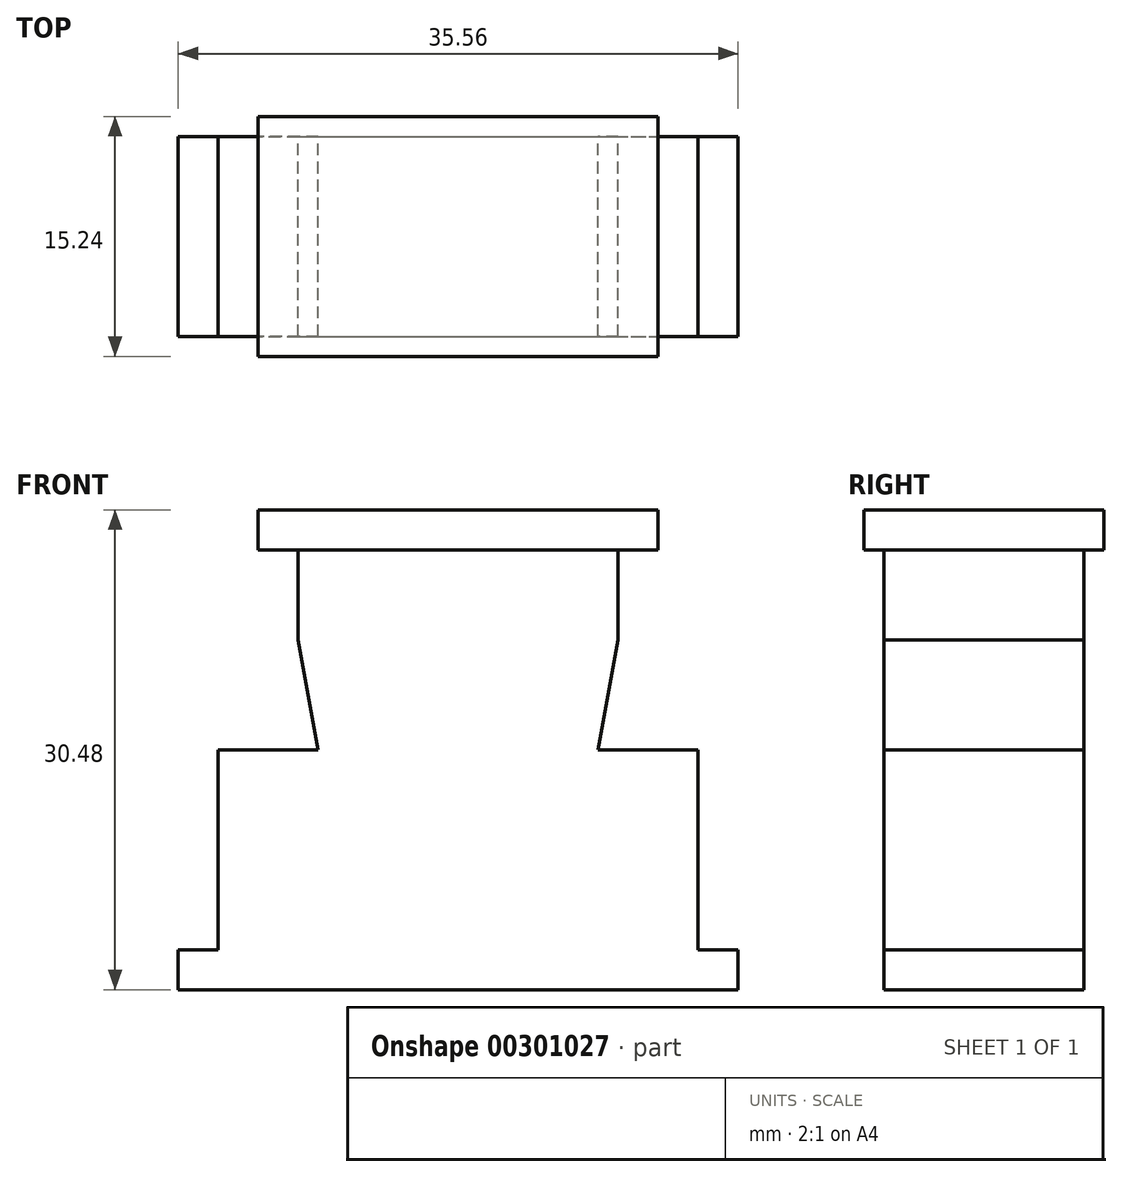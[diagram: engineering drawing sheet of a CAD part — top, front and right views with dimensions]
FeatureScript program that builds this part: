
annotation { "Feature Type Name" : "Feature", "Feature Type Description" : "" }
export const myFeature = defineFeature(function(context is Context, id is Id, definition is map)
    precondition{}
    {
        {
            var Q0;
            Q0=qCreatedBy(makeId("Front.planeOp"),FACE);
            var sketch = newSketch(context, id + "F0", { "sketchPlane" : qUnion([Q0])});
            skLineSegment(sketch, "E0.bottom", {"start": v(0, 19.46) * mm, "end": v(-25.4, 19.46) * mm});
            skLineSegment(sketch, "E0.top", {"start": v(0, 16.92) * mm, "end": v(-25.4, 16.92) * mm});
            skLineSegment(sketch, "E0.left", {"start": v(0, 19.46) * mm, "end": v(0, 16.92) * mm});
            skLineSegment(sketch, "E0.right", {"start": v(-25.4, 19.46) * mm, "end": v(-25.4, 16.92) * mm});
            skLineSegment(sketch, "E1", {"start": v(-12.7, 16.92) * mm, "end": v(-12.7, -8.48) * mm});
            skLineSegment(sketch, "E2", {"start": v(-12.7, -8.48) * mm, "end": v(-12.7, 4.22) * mm});
            skLineSegment(sketch, "E3", {"start": v(-22.86, 11.2) * mm, "end": v(-2.54, 11.2) * mm});
            skPoint(sketch, "E4", {"position": v(-12.7, 11.2) * mm});
            skLineSegment(sketch, "E5", {"start": v(-12.7, -8.48) * mm, "end": v(-30.48, -8.48) * mm});
            skLineSegment(sketch, "E6", {"start": v(-30.48, -8.48) * mm, "end": v(5.08, -8.48) * mm});
            skLineSegment(sketch, "E7", {"start": v(-30.48, -8.48) * mm, "end": v(-30.48, -11.02) * mm});
            skLineSegment(sketch, "E8", {"start": v(-30.48, -11.02) * mm, "end": v(5.07, -11.02) * mm});
            skLineSegment(sketch, "E9", {"start": v(5.07, -11.02) * mm, "end": v(5.08, -8.48) * mm});
            skLineSegment(sketch, "E10", {"start": v(-21.59, 4.22) * mm, "end": v(-12.7, 4.22) * mm});
            skLineSegment(sketch, "E11", {"start": v(-3.81, 4.22) * mm, "end": v(-21.59, 4.22) * mm});
            skLineSegment(sketch, "E12", {"start": v(-22.86, 11.2) * mm, "end": v(-21.59, 4.22) * mm});
            skLineSegment(sketch, "E13", {"start": v(-2.54, 11.2) * mm, "end": v(-3.81, 4.22) * mm});
            skLineSegment(sketch, "E14", {"start": v(-3.81, 4.22) * mm, "end": v(2.54, 4.22) * mm});
            skLineSegment(sketch, "E15", {"start": v(-22.86, 11.2) * mm, "end": v(-22.86, 16.92) * mm});
            skLineSegment(sketch, "E16", {"start": v(-2.54, 11.2) * mm, "end": v(-2.54, 16.92) * mm});
            skLineSegment(sketch, "E17", {"start": v(-21.59, 4.22) * mm, "end": v(-27.94, 4.22) * mm});
            skLineSegment(sketch, "E18", {"start": v(-27.94, 4.22) * mm, "end": v(-27.94, -8.48) * mm});
            skLineSegment(sketch, "E19", {"start": v(2.54, 4.22) * mm, "end": v(2.54, -8.48) * mm});
            skSolve(sketch);
        }
        {
            var Q0;
            Q0 = qSketchRegion(id + "F0", true);
            extrude(context, id + "F1", {"entities" : qUnion([Q0]), "endBound" : BoundingType.SYMMETRIC, "depth" : 12.7 * mm});
        }
        {
            var Q0;
            Q0=makeQuery(id+"F0.imprint","IMPRINT",FACE,{"disambiguationData":[TD([[makeQuery(id+"F0.imprint","IMPRINT",EDGE,{"derivedFrom":sQuery(id+"F0.wireOp",EDGE,"E0.bottom")}),1.0]])]});
            extrude(context, id + "F2", {"entities" : qUnion([Q0]), "operationType" : NewBodyOperationType.ADD, "endBound" : BoundingType.SYMMETRIC, "depth" : 15.24 * mm});
        }
    });
